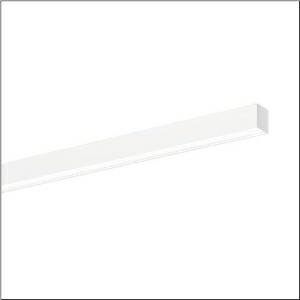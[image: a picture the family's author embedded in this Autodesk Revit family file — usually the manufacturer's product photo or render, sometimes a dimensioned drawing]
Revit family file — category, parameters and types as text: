
# Revit family: silica_r__21_51mx23da44wb_8e2d
name_source: partatom
category: Lighting Fixtures
units: mm (PartAtom-declared; Revit-internal decimal feet)

## family parameters
Cut with Voids When Loaded = No
Host = Face
Light Source = No
Part Type = Normal
Room Calculation Point = No
Round Connector Dimension = Use Diameter
Shared = No

## types (1)
- --- (1 x LED, 3280 lm, 22.4 W, 4000K)
    Apparent Load = 22 VA
    CIE Flux Codes = 78 96 99 100 100
    Color Rendering = 80
    Color Temperature = 4000K
    Default Elevation = 1800 mm
    Description = Silica® 21, office luminaire, primary optical cover: prismatic diffuser, of PMMA, CAT 2 (L<= 3000cd/m²), light emission: direct distribution, primary light characteristic: symmetric, installation type: surface-mounted, LED, rated luminous flux: 3.280lm, luminous efficacy: 146lm/W, light colour: 840, colour temperature: 4000K, control gear: DALI 2, with terminal, 3+2-pole, max. 2.5mm², mains connection: 220..240V, AC, 50/60Hz, rated input power: 22.4W, luminaire housing, of aluminium, traffic white (RAL 9016), length: 1.204mm, width: 53mm, height: 53mm, protection rating (complete): IP20, insulation class (complete): insulation class I (protective earthing), certification: CE, permissible operating ambient temperature: 0..+35°C, standard: EN 50419, packaging unit: 1 piece
    Height = 53 mm
    Lamp = 1 x LED
    Lamp Light Flux = 3280 lm
    Lamp Power = 22.4 W
    Lamp count = 1
    Length = 1204 mm
    Luminous efficacy = 146 lm/W
    Manufacturer = Siteco
    ModVariant = No
    Model = 51MX23DA44WB
    Mounting Place = Ceiling
    Mounting Type = Surface mounted
    Number of Poles = 1
    OnlyDefault = Yes
    Power Factor = 1
    Product Name = Silica® 21
    Product group = office luminaire | ceiling mounted
    ProductGroupID = 302
    Protection Class = Protection class I
    Protection Degree = IP 20
    RLX_Detail_Level = 1
    RLX_Emergency_Light_Flux = 0 lm
    RLX_Emergency_Type = 0
    RLX_Emergency_Type_DB = No
    RlxData = <blob elided: 18865 chars, md5=42f30b54>
    Socket = socket
    Standby Power = 0 W
    System Light Flux = 3280 lm
    System Power = 22 W
    Type Comments = factory setting: luminous flux: 100 % | dim-lin: 254 | 323 mA
    Type Image = l_1335877.jpg
    URL = http://relux.com
    VarID = @adj_008037
    Voltage = 0 V
    Weight = 0.00 kg
    Width = 53 mm

## geometry (parser evidence)
native form markers: Blend x4, Sweep x11
no freeform markers — native parametric forms only
